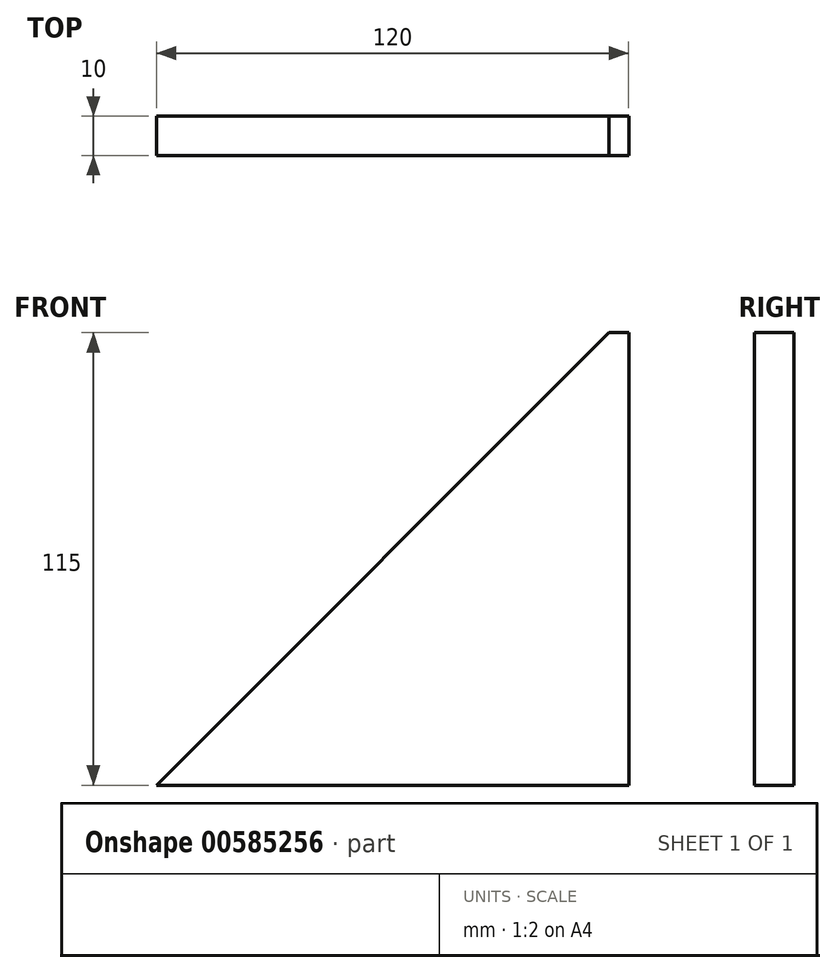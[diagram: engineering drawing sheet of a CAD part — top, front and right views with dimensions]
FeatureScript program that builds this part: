
annotation { "Feature Type Name" : "Feature", "Feature Type Description" : "" }
export const myFeature = defineFeature(function(context is Context, id is Id, definition is map)
    precondition{}
    {
        {
            var Q0;
            Q0=qCreatedBy(makeId("Front.planeOp"),FACE);
            var sketch = newSketch(context, id + "F0", { "sketchPlane" : qUnion([Q0])});
            skLineSegment(sketch, "E0", {"start": v(44.13, 62.57) * mm, "end": v(-70.87, -52.43) * mm});
            skLineSegment(sketch, "E1", {"start": v(44.13, 62.57) * mm, "end": v(44.13, -52.43) * mm});
            skLineSegment(sketch, "E2", {"start": v(-70.87, -52.43) * mm, "end": v(44.13, -52.43) * mm});
            skLineSegment(sketch, "E3", {"start": v(44.13, 62.57) * mm, "end": v(49.13, 62.57) * mm});
            skLineSegment(sketch, "E4", {"start": v(49.13, 62.57) * mm, "end": v(49.13, -52.43) * mm});
            skLineSegment(sketch, "E5", {"start": v(49.13, -52.43) * mm, "end": v(44.13, -52.43) * mm});
            skSolve(sketch);
        }
        {
            var Q0;
            Q0=makeQuery(id+"F0.imprint","IMPRINT",FACE,{"disambiguationData":[TD([[makeQuery(id+"F0.imprint","IMPRINT",EDGE,{"derivedFrom":sQuery(id+"F0.wireOp",EDGE,"E1")}),1.0]])]});
            var Q1;
            Q1=makeQuery(id+"F0.imprint","IMPRINT",FACE,{"disambiguationData":[TD([[makeQuery(id+"F0.imprint","IMPRINT",EDGE,{"derivedFrom":sQuery(id+"F0.wireOp",EDGE,"E0")}),1.0]])]});
            extrude(context, id + "F1", {"entities" : qUnion([Q0, Q1]), "depth" : 10 * mm, "offsetDistance" : 25 * mm});
        }
    });
